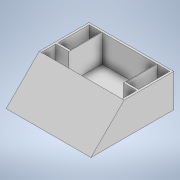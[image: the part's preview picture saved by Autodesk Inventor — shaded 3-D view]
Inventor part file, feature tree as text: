
AUTODESK INVENTOR PART (.ipt)
format: ipt  version: 2020 (Build 240168000, 168)  size: 138,752 bytes
history: native  units: mm
features: extrude x4, sketch x4, chamfer x1
ambient origin geometry x8: Origin, YZ Plane, XZ Plane, XY Plane, X Axis, Y Axis, Z Axis, Center Point
bodies: Body1 (feature_tree)
feature tree (9):
  extrude  "Extrusão2"  Depth=80.0mm
  extrude  "Extrusão3"  TaperAngle=0.0deg  [1 undecoded]
  extrude  "Extrusão4"  Depth=1.6mm
  extrude  "Extrusão5"  Depth=66.25mm TaperAngle=0.0deg
  chamfer  "Chanfro1"  Distance=80.0mm Angle=45.0deg
  sketch  "Esboço3"  dims[d4=204.6mm d5=80.0mm]
  sketch  "Esboço7"  dims[d6=200.0mm d7=0.0mm d26=0.0mm d27=0.0mm]
  sketch  "Esboço8"  dims[d29=1.6mm d30=1.6mm]
  sketch  "Esboço9"  dims[d31=66.25mm d32=0.0mm d40=66.25mm d41=0.0mm d42=80.0mm d43=2.0mm d44=45.0deg]
note: 1 required parameter value undecoded (feature->parameter linkage not recoverable at this tier; creation-order binding heuristic only, values carry confidence <= 0.55)
